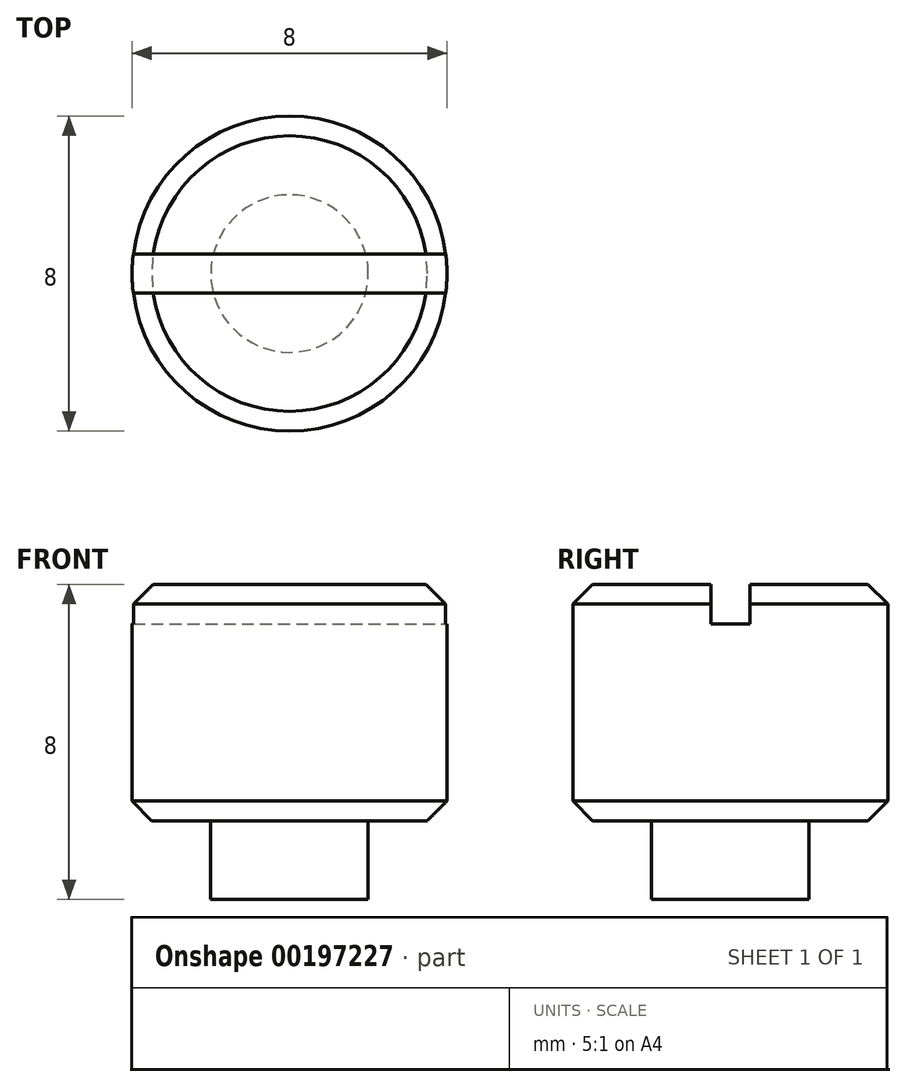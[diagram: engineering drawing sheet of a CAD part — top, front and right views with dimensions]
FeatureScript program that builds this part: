
annotation { "Feature Type Name" : "Feature", "Feature Type Description" : "" }
export const myFeature = defineFeature(function(context is Context, id is Id, definition is map)
    precondition{}
    {
        {
            var Q0;
            Q0=qCreatedBy(makeId("Front.planeOp"),FACE);
            var sketch = newSketch(context, id + "F0", { "sketchPlane" : qUnion([Q0])});
            skLineSegment(sketch, "E0", {"start": v(0, 0) * mm, "end": v(2, 0) * mm});
            skLineSegment(sketch, "E1", {"start": v(2, 0) * mm, "end": v(2, 2) * mm});
            skLineSegment(sketch, "E2", {"start": v(2, 2) * mm, "end": v(4, 2) * mm});
            skLineSegment(sketch, "E3", {"start": v(4, 2) * mm, "end": v(4, 8) * mm});
            skLineSegment(sketch, "E4", {"start": v(4, 8) * mm, "end": v(0, 8) * mm});
            skLineSegment(sketch, "E5", {"start": v(0, 8) * mm, "end": v(0, 0) * mm});
            skSolve(sketch);
        }
        {
            var Q0;
            Q0=makeQuery(id+"F0.imprint","IMPRINT",FACE,{"disambiguationData":[TD([[makeQuery(id+"F0.imprint","IMPRINT",EDGE,{"derivedFrom":sQuery(id+"F0.wireOp",EDGE,"E0")}),1.0]])]});
            var Q1;
            Q1=sQuery(id+"F0.wireOp",EDGE,"E5");
            revolve(context, id + "F1", {"entities" : qUnion([Q0]), "axis" : qUnion([Q1]), "revolveType" : RevolveType.FULL});
        }
        {
            var Q0;
            Q0=makeQuery(id+"F1.opRevolve","SWEPT_EDGE",EDGE,{"disambiguationData":[OSD([sQuery(id+"F0.wireOp",EDGE,"E3"),sQuery(id+"F0.wireOp",EDGE,"E4")])]});
            chamfer(context, id + "F2", {"entities" : qUnion([Q0]), "width" : 0.5 * mm, "tangentPropagation" : true});
        }
        {
            var Q0;
            Q0=makeQuery(id+"F1.opRevolve","SWEPT_EDGE",EDGE,{"disambiguationData":[OSD([sQuery(id+"F0.wireOp",EDGE,"E2"),sQuery(id+"F0.wireOp",EDGE,"E3")])]});
            chamfer(context, id + "F3", {"entities" : qUnion([Q0]), "width" : 0.5 * mm, "tangentPropagation" : true});
        }
        {
            var Q0;
            Q0=makeQuery(id+"F1.opRevolve","SWEPT_FACE",FACE,{"disambiguationData":[OSD([sQuery(id+"F0.wireOp",EDGE,"E4")])]});
            var sketch = newSketch(context, id + "F4", { "sketchPlane" : qUnion([Q0])});
            skLineSegment(sketch, "E6", {"start": v(0, 0) * mm, "end": v(-5, 0) * mm});
            skLineSegment(sketch, "E7", {"start": v(-5, 0) * mm, "end": v(-5, -0.5) * mm});
            skLineSegment(sketch, "E8", {"start": v(-5, -0.5) * mm, "end": v(5, -0.5) * mm});
            skLineSegment(sketch, "E9", {"start": v(5, -0.5) * mm, "end": v(5, 0) * mm});
            skLineSegment(sketch, "E10", {"start": v(5, 0) * mm, "end": v(5, 0.5) * mm});
            skLineSegment(sketch, "E11", {"start": v(5, 0.5) * mm, "end": v(-5, 0.5) * mm});
            skLineSegment(sketch, "E12", {"start": v(-5, 0.5) * mm, "end": v(-5, 0) * mm});
            skSolve(sketch);
        }
        {
            var Q0;
            {var subQ5=sQuery(id+"F4.wireOp",EDGE,"E9");Q0=makeQuery(id+"F4.imprint","IMPRINT",FACE,{"disambiguationData":[TD([[makeQuery(id+"F4.imprint","IMPRINT",EDGE,{"derivedFrom":subQ5}),1.0]])]});}
            var Q1;
            {var subQ0=sQuery(id+"F0.wireOp",EDGE,"E4");var subQ1=makeQuery(id+"F2.opChamfer","BLEND_EDGE",EDGE,{"blendedFrom":[makeQuery(id+"F1.opRevolve","SWEPT_EDGE",EDGE,{"disambiguationData":[OSD([sQuery(id+"F0.wireOp",EDGE,"E3"),subQ0])]}),makeQuery(id+"F1.opRevolve","SWEPT_FACE",FACE,{"disambiguationData":[OSD([subQ0])]})],"blendedInto":[makeQuery(id+"F1.opRevolve","SWEPT_FACE",FACE,{"disambiguationData":[OSD([subQ0])]})]});var subQ6=sQuery(id+"F4.wireOp",EDGE,"E8");var subQ7=makeQuery(id+"F4.imprint","INTERSECT",VERTEX,{"disambiguationData":[OD(0.0)],"derivedFrom":[subQ1,subQ6]});Q1=makeQuery(id+"F4.imprint","IMPRINT",FACE,{"disambiguationData":[TD([[makeQuery(id+"F4.imprint","IMPRINT",EDGE,{"disambiguationData":[TD([[subQ7,-1.0]])],"derivedFrom":subQ6}),1.0]])]});}
            var Q2;
            {var subQ0=sQuery(id+"F4.wireOp",EDGE,"E7");Q2=makeQuery(id+"F4.imprint","IMPRINT",FACE,{"disambiguationData":[TD([[makeQuery(id+"F4.imprint","IMPRINT",EDGE,{"derivedFrom":subQ0}),1.0]])]});}
            var Q3;
            {var subQ0=sQuery(id+"F4.wireOp",EDGE,"E12");Q3=makeQuery(id+"F4.imprint","IMPRINT",FACE,{"disambiguationData":[TD([[makeQuery(id+"F4.imprint","IMPRINT",EDGE,{"derivedFrom":subQ0}),1.0]])]});}
            extrude(context, id + "F5", {"entities" : qUnion([Q0, Q1, Q2, Q3]), "operationType" : NewBodyOperationType.REMOVE, "oppositeDirection" : true, "depth" : 1 * mm});
        }
    });
